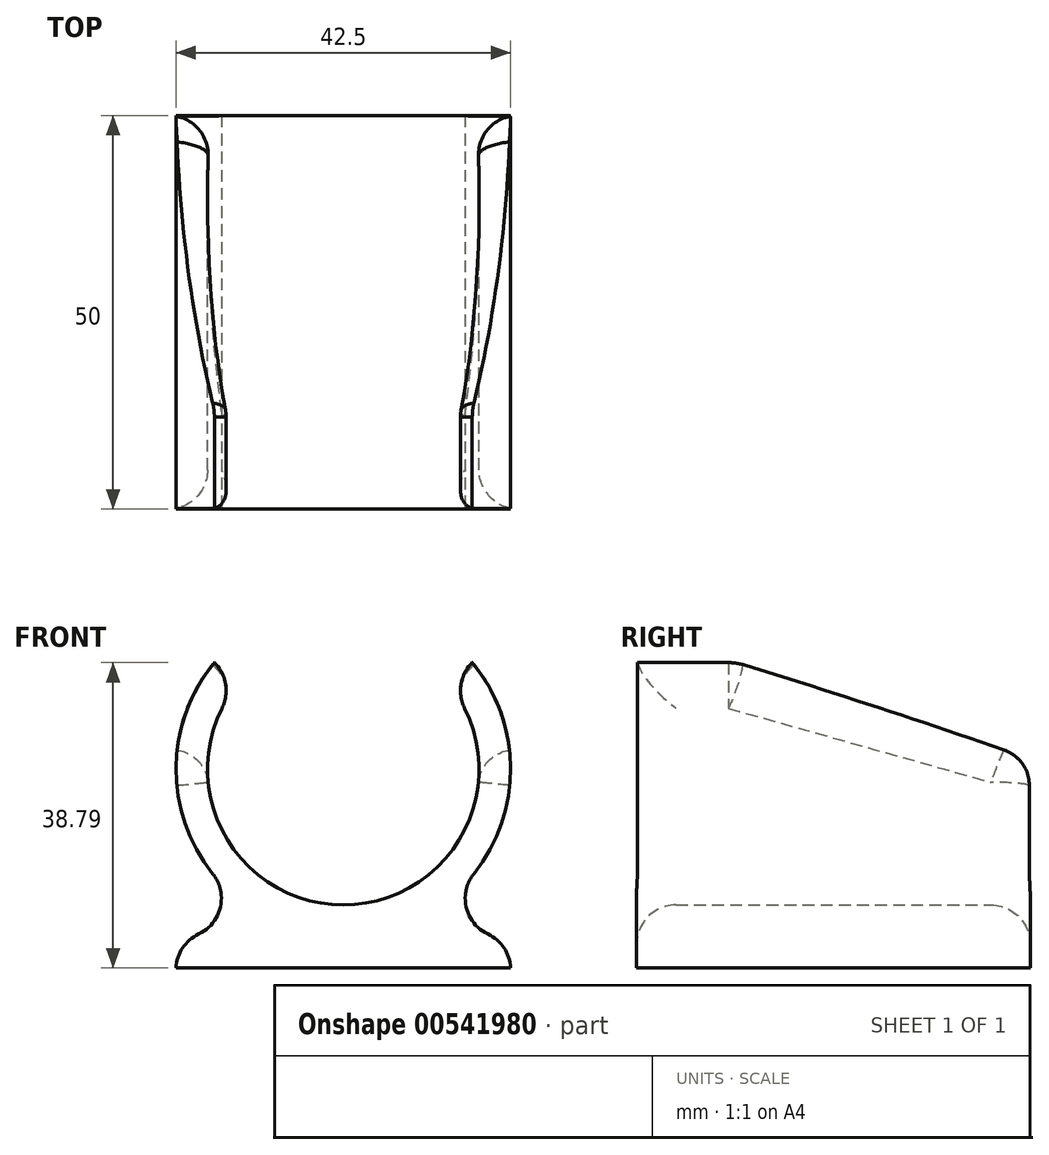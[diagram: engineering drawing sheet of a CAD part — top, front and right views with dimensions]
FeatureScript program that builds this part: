
annotation { "Feature Type Name" : "Feature", "Feature Type Description" : "" }
export const myFeature = defineFeature(function(context is Context, id is Id, definition is map)
    precondition{}
    {
        {
            var Q0;
            Q0=qCreatedBy(makeId("Front.planeOp"),FACE);
            var sketch = newSketch(context, id + "F0", { "sketchPlane" : qUnion([Q0])});
            skCircle(sketch, "E0", {"center": v(0, 0) * mm, "radius": 17.25 * mm});
            skCircle(sketch, "E1", {"center": v(0, 0) * mm, "radius": 21.25 * mm});
            skLineSegment(sketch, "E2", {"start": v(0, 0) * mm, "end": v(0, -21.25) * mm, "construction": true});
            skLineSegment(sketch, "E3", {"start": v(0, -21.25) * mm, "end": v(0, -25.25) * mm});
            skLineSegment(sketch, "E4", {"start": v(0, 0) * mm, "end": v(-21.25, 0) * mm, "construction": true});
            skLineSegment(sketch, "E5", {"start": v(-21.25, -21.25) * mm, "end": v(-21.25, -25.25) * mm});
            skLineSegment(sketch, "E6", {"start": v(0, 0) * mm, "end": v(21.25, 0) * mm, "construction": true});
            skLineSegment(sketch, "E7", {"start": v(21.25, -21.25) * mm, "end": v(21.25, -25.25) * mm});
            skLineSegment(sketch, "E8", {"start": v(0, -25.25) * mm, "end": v(-21.25, -25.25) * mm});
            skLineSegment(sketch, "E9", {"start": v(0, -25.25) * mm, "end": v(21.25, -25.25) * mm});
            skLineSegment(sketch, "E10", {"start": v(0, -21.25) * mm, "end": v(-21.25, -21.25) * mm});
            skLineSegment(sketch, "E11", {"start": v(0, -21.25) * mm, "end": v(21.25, -21.25) * mm});
            skLineSegment(sketch, "E12", {"start": v(-12.52, -17.17) * mm, "end": v(-12.52, -21.25) * mm, "construction": true});
            skLineSegment(sketch, "E13", {"start": v(12.52, -17.17) * mm, "end": v(12.52, -21.25) * mm, "construction": true});
            skArc(sketch, "E14", {"start": v(-21.25, -21.25) * mm, "mid": v(-16.43, -20.18) * mm, "end": v(-12.52, -17.17) * mm});
            skArc(sketch, "E15", {"start": v(12.52, -17.17) * mm, "mid": v(16.43, -20.18) * mm, "end": v(21.25, -21.25) * mm});
            skSolve(sketch);
        }
        {
            var Q0;
            Q0=makeQuery(id+"F0.imprint","IMPRINT",FACE,{"disambiguationData":[TD([[makeQuery(id+"F0.imprint","IMPRINT",EDGE,{"derivedFrom":sQuery(id+"F0.wireOp",EDGE,"E0")}),-1.0]])]});
            var Q1;
            {var subQ0=sQuery(id+"F0.wireOp",EDGE,"E10");Q1=makeQuery(id+"F0.imprint","IMPRINT",FACE,{"disambiguationData":[TD([[makeQuery(id+"F0.imprint","IMPRINT",EDGE,{"derivedFrom":subQ0}),-1.0]])]});}
            var Q2;
            {var subQ0=sQuery(id+"F0.wireOp",EDGE,"E11");Q2=makeQuery(id+"F0.imprint","IMPRINT",FACE,{"disambiguationData":[TD([[makeQuery(id+"F0.imprint","IMPRINT",EDGE,{"derivedFrom":subQ0}),1.0]])]});}
            var Q3;
            Q3=makeQuery(id+"F0.imprint","IMPRINT",FACE,{"disambiguationData":[TD([[makeQuery(id+"F0.imprint","IMPRINT",EDGE,{"derivedFrom":sQuery(id+"F0.wireOp",EDGE,"E3")}),-1.0]])]});
            var Q4;
            Q4=makeQuery(id+"F0.imprint","IMPRINT",FACE,{"disambiguationData":[TD([[makeQuery(id+"F0.imprint","IMPRINT",EDGE,{"derivedFrom":sQuery(id+"F0.wireOp",EDGE,"E3")}),1.0]])]});
            extrude(context, id + "F1", {"entities" : qUnion([Q0, Q1, Q2, Q3, Q4]), "depth" : 50 * mm, "offsetDistance" : 25 * mm});
        }
        {
            var Q0;
            Q0=qCreatedBy(makeId("Front.planeOp"),FACE);
            var sketch = newSketch(context, id + "F2", { "sketchPlane" : qUnion([Q0])});
            skLineSegment(sketch, "E16", {"start": v(0, 0) * mm, "end": v(-61.93, 51.2) * mm});
            skLineSegment(sketch, "E17", {"start": v(-61.93, 51.2) * mm, "end": v(61.93, 51.2) * mm});
            skLineSegment(sketch, "E18", {"start": v(61.93, 51.2) * mm, "end": v(0, 0) * mm});
            skSolve(sketch);
        }
        {
            var Q0;
            Q0=qSketchRegion(id+"F2",true);
            extrude(context, id + "F3", {"entities" : qUnion([Q0]), "operationType" : NewBodyOperationType.REMOVE, "depth" : 70 * mm, "offsetDistance" : 25 * mm});
        }
        {
            var Q0;
            Q0=makeQuery(id+"F1.opExtrude","CAP_EDGE",EDGE,{"disambiguationData":[OSD([sQuery(id+"F0.wireOp",EDGE,"E0")])],"isStart":false});
            var Q1;
            Q1=makeQuery(id+"F1.opExtrude","CAP_EDGE",EDGE,{"disambiguationData":[OSD([sQuery(id+"F0.wireOp",EDGE,"E0")])],"isStart":true});
            var Q2;
            Q2=makeQuery(id+"F3.boolean.opBoolean","INTERSECT",EDGE,{"derivedFrom":[makeQuery(id+"F1.opExtrude","SWEPT_FACE",FACE,{"disambiguationData":[OSD([sQuery(id+"F0.wireOp",EDGE,"E0")])]}),makeQuery(id+"F3.opExtrude","SWEPT_FACE",FACE,{"disambiguationData":[OSD([sQuery(id+"F2.wireOp",EDGE,"E16")])]})]});
            var Q3;
            Q3=makeQuery(id+"F3.boolean.opBoolean","INTERSECT",EDGE,{"derivedFrom":[makeQuery(id+"F1.opExtrude","SWEPT_FACE",FACE,{"disambiguationData":[OSD([sQuery(id+"F0.wireOp",EDGE,"E0")])]}),makeQuery(id+"F3.opExtrude","SWEPT_FACE",FACE,{"disambiguationData":[OSD([sQuery(id+"F2.wireOp",EDGE,"E18")])]})]});
            var Q4;
            Q4=makeQuery(id+"F1.opExtrude","SWEPT_EDGE",EDGE,{"disambiguationData":[OSD([sQuery(id+"F0.wireOp",EDGE,"E5"),sQuery(id+"F0.wireOp",EDGE,"E10"),sQuery(id+"F0.wireOp",EDGE,"E14")])]});
            var Q5;
            Q5=makeQuery(id+"F1.opExtrude","SWEPT_EDGE",EDGE,{"disambiguationData":[OSD([sQuery(id+"F0.wireOp",EDGE,"E7"),sQuery(id+"F0.wireOp",EDGE,"E11"),sQuery(id+"F0.wireOp",EDGE,"E15")])]});
            fillet(context, id + "F4", {"entities" : qUnion([Q0, Q1, Q2, Q3, Q4, Q5]), "radius" : 5 * mm, "tangentPropagation" : true, "allowEdgeOverflow" : false});
        }
        {
            var Q0;
            Q0=makeQuery(id+"F1.opExtrude","SWEPT_EDGE",EDGE,{"disambiguationData":[OSD([sQuery(id+"F0.wireOp",EDGE,"E1"),sQuery(id+"F0.wireOp",EDGE,"E15")])]});
            var Q1;
            Q1=makeQuery(id+"F1.opExtrude","SWEPT_EDGE",EDGE,{"disambiguationData":[OSD([sQuery(id+"F0.wireOp",EDGE,"E1"),sQuery(id+"F0.wireOp",EDGE,"E14")])]});
            fillet(context, id + "F5", {"entities" : qUnion([Q0, Q1]), "radius" : 5 * mm, "tangentPropagation" : true, "allowEdgeOverflow" : false});
        }
        {
            var Q0;
            Q0=qCreatedBy(makeId("Top.planeOp"),FACE);
            var Q1;
            Q1=makeQuery(id+"F1.opExtrude","CAP_EDGE",EDGE,{"disambiguationData":[OSD([sQuery(id+"F0.wireOp",EDGE,"E8"),sQuery(id+"F0.wireOp",EDGE,"E9")])],"isStart":true});
            cPlane(context, id + "F6", {"entities" : qUnion([Q0, Q1]), "cplaneType" : CPlaneType.LINE_ANGLE, "offset" : 25 * mm, "angle" : 20 * degree, "width" : 150 * mm, "height" : 150 * mm});
        }
        {
            var Q0;
            Q0=qCreatedBy(id+"F6.planeOp",FACE);
            cPlane(context, id + "F7", {"entities" : qUnion([Q0]), "cplaneType" : CPlaneType.OFFSET, "offset" : 25 * mm, "oppositeDirection" : true, "width" : 150 * mm, "height" : 150 * mm});
        }
        {
            var Q0;
            Q0=qCreatedBy(id+"F7.planeOp",FACE);
            var sketch = newSketch(context, id + "F8", { "sketchPlane" : qUnion([Q0])});
            skLineSegment(sketch, "E19.bottom", {"start": v(-24.4, -18.79) * mm, "end": v(79.49, -18.79) * mm});
            skLineSegment(sketch, "E19.top", {"start": v(-24.4, 52.13) * mm, "end": v(79.49, 52.13) * mm});
            skLineSegment(sketch, "E19.left", {"start": v(-24.4, -18.79) * mm, "end": v(-24.4, 52.13) * mm});
            skLineSegment(sketch, "E19.right", {"start": v(79.49, -18.79) * mm, "end": v(79.49, 52.13) * mm});
            skSolve(sketch);
        }
        {
            var Q0;
            Q0 = qSketchRegion(id + "F8", true);
            extrude(context, id + "F9", {"entities" : qUnion([Q0]), "operationType" : NewBodyOperationType.REMOVE, "oppositeDirection" : true, "depth" : 25 * mm, "offsetDistance" : 25 * mm});
        }
        {
            var Q0;
            Q0=makeQuery(id+"F9.boolean.opBoolean","INTERSECT",EDGE,{"derivedFrom":[makeQuery(id+"F4.opFillet","BLEND_FACE",FACE,{"disambiguationData":[OSD([sQuery(id+"F0.wireOp",EDGE,"E0"),sQuery(id+"F2.wireOp",EDGE,"E18")])]}),makeQuery(id+"F9.opExtrude","CAP_FACE",FACE,{"disambiguationData":[OSD([sQuery(id+"F8.wireOp",EDGE,"E19.bottom"),sQuery(id+"F8.wireOp",EDGE,"E19.top"),sQuery(id+"F8.wireOp",EDGE,"E19.left"),sQuery(id+"F8.wireOp",EDGE,"E19.right")])],"isStart":true})]});
            var Q1;
            Q1=makeQuery(id+"F9.boolean.opBoolean","INTERSECT",EDGE,{"derivedFrom":[makeQuery(id+"F4.opFillet","BLEND_FACE",FACE,{"disambiguationData":[OSD([sQuery(id+"F0.wireOp",EDGE,"E0"),sQuery(id+"F2.wireOp",EDGE,"E16")])]}),makeQuery(id+"F9.opExtrude","CAP_FACE",FACE,{"disambiguationData":[OSD([sQuery(id+"F8.wireOp",EDGE,"E19.bottom"),sQuery(id+"F8.wireOp",EDGE,"E19.top"),sQuery(id+"F8.wireOp",EDGE,"E19.left"),sQuery(id+"F8.wireOp",EDGE,"E19.right")])],"isStart":true})]});
            fillet(context, id + "F10", {"entities" : qUnion([Q0, Q1]), "radius" : 5 * mm, "tangentPropagation" : true, "allowEdgeOverflow" : false});
        }
    });
